# Revit family: Wok SKWi
name_source: partatom
category: Specialty Equipment
units: mm (PartAtom-declared; Revit-internal decimal feet)

## family parameters
Always vertical = Yes
Cut with Voids When Loaded = No
Enable Cutting in Views = No
Maintain Annotation Orientation = No
OmniClass Number = 23.40.40.14.17.17
OmniClass Title = Ranges
Part Type = Normal
Room Calculation Point = No
Round Connector Dimension = Use Diameter
Shared = No
Work Plane-Based = No

## types (1)
- SKWi - Induction Wok
    Default Elevation = 0 mm  [stored 0 ft]
    Depth = 650 mm  [stored 2.13255 ft]
    Description = Induction Wok
    Elec Conn RI Height = 0 mm  [stored 0 ft]
    FL Amps = 15 A
    Height = 310 mm
    Manufacturer = ADVENTYS
    Model = SKWi
    Phase = 1
    Volts = 240 V
    Watts = 3600 W
    Width = 400 mm  [stored 1.31234 ft]

note: [stored X ft] marks values corroborated as IEEE doubles in the binary element streams (Revit-internal decimal feet)

## geometry (parser evidence)
native form markers: Blend x8, Sweep x2
no freeform markers — native parametric forms only
